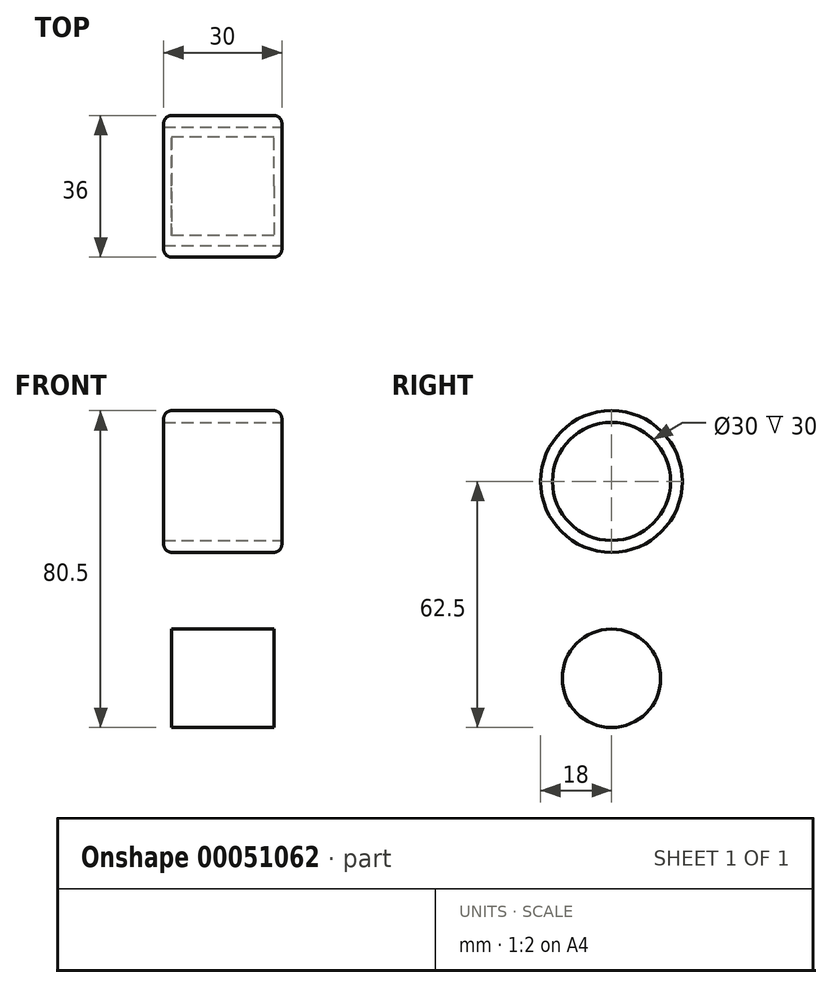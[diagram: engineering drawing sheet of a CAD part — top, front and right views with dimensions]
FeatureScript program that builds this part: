
annotation { "Feature Type Name" : "Feature", "Feature Type Description" : "" }
export const myFeature = defineFeature(function(context is Context, id is Id, definition is map)
    precondition{}
    {
        {
            var Q0;
            Q0=qCreatedBy(makeId("Front.planeOp"),FACE);
            var sketch = newSketch(context, id + "F0", { "sketchPlane" : qUnion([Q0])});
            skLineSegment(sketch, "E0", {"start": v(13, 0) * mm, "end": v(13, -80) * mm});
            skLineSegment(sketch, "E1", {"start": v(-13, 0) * mm, "end": v(-13, -80) * mm});
            skLineSegment(sketch, "E2", {"start": v(-10, 0) * mm, "end": v(-10, -80) * mm});
            skLineSegment(sketch, "E3", {"start": v(10, 0) * mm, "end": v(10, -80) * mm});
            skLineSegment(sketch, "E4", {"start": v(0, 0) * mm, "end": v(-10, 0) * mm});
            skLineSegment(sketch, "E5", {"start": v(10, 0) * mm, "end": v(0, 0) * mm});
            skLineSegment(sketch, "E6", {"start": v(13, 0) * mm, "end": v(-10, 0) * mm});
            skLineSegment(sketch, "E7", {"start": v(10, 0) * mm, "end": v(-13, 0) * mm});
            skPoint(sketch, "E8", {"position": v(0, -76) * mm});
            skLineSegment(sketch, "E9", {"start": v(13, -80) * mm, "end": v(10, -80) * mm});
            skLineSegment(sketch, "E10", {"start": v(-10, -80) * mm, "end": v(-13, -80) * mm});
            skFitSpline(sketch, "E11", {"points": [v(-10, -80) * mm, v(0, -70) * mm, v(10, -80) * mm], "startDerivative": vector(24, 28) * mm, "endDerivative": vector(24, -28) * mm});
            skSolve(sketch);
        }
        {
            var Q0;
            Q0=makeQuery(id+"F0.imprint","IMPRINT",FACE,{"disambiguationData":[TD([[makeQuery(id+"F0.imprint","IMPRINT",EDGE,{"derivedFrom":sQuery(id+"F0.wireOp",EDGE,"E0")}),-1.0]])]});
            var Q1;
            {var subQ0=sQuery(id+"F0.wireOp",EDGE,"E2");Q1=makeQuery(id+"F0.imprint","IMPRINT",FACE,{"disambiguationData":[TD([[makeQuery(id+"F0.imprint","IMPRINT",EDGE,{"derivedFrom":subQ0}),1.0]])]});}
            var Q2;
            {var subQ0=sQuery(id+"F0.wireOp",EDGE,"E1");Q2=makeQuery(id+"F0.imprint","IMPRINT",FACE,{"disambiguationData":[TD([[makeQuery(id+"F0.imprint","IMPRINT",EDGE,{"derivedFrom":subQ0}),1.0]])]});}
            var Q3;
            Q3=sQuery(id+"F0.wireOp",EDGE,"E7");
            revolve(context, id + "F1", {"entities" : qUnion([Q0, Q1, Q2]), "axis" : qUnion([Q3]), "revolveType" : RevolveType.FULL});
        }
        {
            var Q0;
            Q0=makeQuery(id+"F1.opRevolve","SWEPT_FACE",FACE,{"disambiguationData":[OSD([sQuery(id+"F0.wireOp",EDGE,"E1")])]});
            var sketch = newSketch(context, id + "F2", { "sketchPlane" : qUnion([Q0])});
            skCircle(sketch, "E12", {"center": v(0, 50) * mm, "radius": 12.5 * mm});
            skCircle(sketch, "E13.MirrorC", {"center": v(0, -50) * mm, "radius": 12.5 * mm});
            skCircle(sketch, "E14", {"center": v(-43.3, 25) * mm, "radius": 12.5 * mm});
            skCircle(sketch, "E15", {"center": v(43.3, 25) * mm, "radius": 12.5 * mm});
            skCircle(sketch, "E16", {"center": v(43.3, -25) * mm, "radius": 12.5 * mm});
            skCircle(sketch, "E17", {"center": v(-43.3, -25) * mm, "radius": 12.5 * mm});
            skSolve(sketch);
        }
        {
            var Q0;
            Q0=makeQuery(id+"F2.imprint","IMPRINT",FACE,{"disambiguationData":[TD([[makeQuery(id+"F2.imprint","IMPRINT",EDGE,{"derivedFrom":sQuery(id+"F2.wireOp",EDGE,"E14")}),1.0]])]});
            var Q1;
            Q1=makeQuery(id+"F2.imprint","IMPRINT",FACE,{"disambiguationData":[TD([[makeQuery(id+"F2.imprint","IMPRINT",EDGE,{"derivedFrom":sQuery(id+"F2.wireOp",EDGE,"E15")}),1.0]])]});
            var Q2;
            Q2=makeQuery(id+"F2.imprint","IMPRINT",FACE,{"disambiguationData":[TD([[makeQuery(id+"F2.imprint","IMPRINT",EDGE,{"derivedFrom":sQuery(id+"F2.wireOp",EDGE,"E16")}),1.0]])]});
            var Q3;
            Q3=makeQuery(id+"F2.imprint","IMPRINT",FACE,{"disambiguationData":[TD([[makeQuery(id+"F2.imprint","IMPRINT",EDGE,{"derivedFrom":sQuery(id+"F2.wireOp",EDGE,"E13.MirrorC")}),-1.0]])]});
            var Q4;
            Q4=makeQuery(id+"F2.imprint","IMPRINT",FACE,{"disambiguationData":[TD([[makeQuery(id+"F2.imprint","IMPRINT",EDGE,{"derivedFrom":sQuery(id+"F2.wireOp",EDGE,"E17")}),1.0]])]});
            var Q5;
            Q5=makeQuery(id+"F2.imprint","IMPRINT",FACE,{"disambiguationData":[TD([[makeQuery(id+"F2.imprint","IMPRINT",EDGE,{"derivedFrom":sQuery(id+"F2.wireOp",EDGE,"E12")}),1.0]])]});
            extrude(context, id + "F3", {"entities" : qUnion([Q0, Q1, Q2, Q3, Q4, Q5]), "operationType" : NewBodyOperationType.REMOVE, "oppositeDirection" : true, "depth" : 119.8 * mm});
        }
        {
            var Q0;
            Q0=makeQuery(id+"F1.opRevolve","SWEPT_FACE",FACE,{"disambiguationData":[OSD([sQuery(id+"F0.wireOp",EDGE,"E1")])]});
            var sketch = newSketch(context, id + "F4", { "sketchPlane" : qUnion([Q0])});
            skCircle(sketch, "E18", {"center": v(0, 0) * mm, "radius": 18 * mm});
            skCircle(sketch, "E19", {"center": v(0, 0) * mm, "radius": 15 * mm});
            skSolve(sketch);
        }
        {
            var Q0;
            Q0=makeQuery(id+"F4.imprint","IMPRINT",FACE,{"disambiguationData":[TD([[makeQuery(id+"F4.imprint","IMPRINT",EDGE,{"derivedFrom":sQuery(id+"F4.wireOp",EDGE,"E19")}),1.0]])]});
            extrude(context, id + "F5", {"entities" : qUnion([Q0]), "operationType" : NewBodyOperationType.REMOVE, "oppositeDirection" : true, "depth" : 102.88 * mm});
        }
        {
            var Q0;
            Q0=makeQuery(id+"F4.imprint","IMPRINT",FACE,{"disambiguationData":[TD([[makeQuery(id+"F4.imprint","IMPRINT",EDGE,{"derivedFrom":sQuery(id+"F4.wireOp",EDGE,"E18")}),1.0]])]});
            extrude(context, id + "F6", {"entities" : qUnion([Q0]), "operationType" : NewBodyOperationType.ADD, "depth" : 2 * mm, "hasSecondDirection" : true, "secondDirectionOppositeDirection" : true, "secondDirectionDepth" : 28 * mm});
        }
        {
            var Q0;
            Q0=makeQuery(id+"F6.opExtrude","CAP_EDGE",EDGE,{"disambiguationData":[OSD([sQuery(id+"F4.wireOp",EDGE,"E18")])],"isStart":false});
            var Q1;
            Q1=makeQuery(id+"F6.opExtrude","CAP_EDGE",EDGE,{"disambiguationData":[OSD([sQuery(id+"F4.wireOp",EDGE,"E18")])],"isStart":true});
            fillet(context, id + "F7", {"entities" : qUnion([Q0, Q1]), "radius" : 2 * mm, "tangentPropagation" : true, "allowEdgeOverflow" : false});
        }
    });
